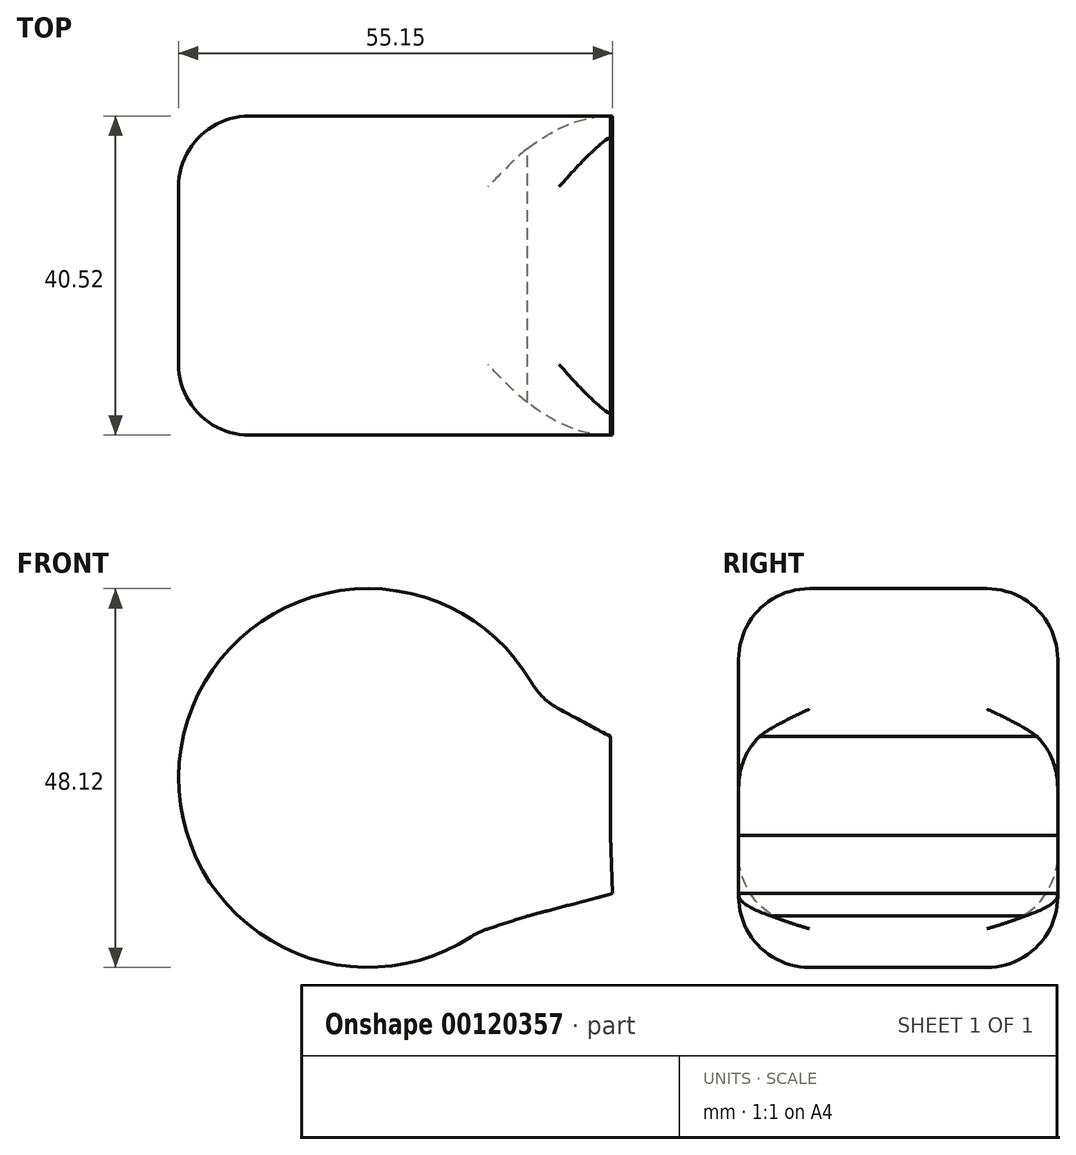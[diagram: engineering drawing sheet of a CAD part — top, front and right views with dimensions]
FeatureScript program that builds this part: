
annotation { "Feature Type Name" : "Feature", "Feature Type Description" : "" }
export const myFeature = defineFeature(function(context is Context, id is Id, definition is map)
    precondition{}
    {
        {
            var Q0;
            Q0=qCreatedBy(makeId("Front.planeOp"),FACE);
            var sketch = newSketch(context, id + "F0", { "sketchPlane" : qUnion([Q0])});
            skCircle(sketch, "E0", {"center": v(0, 0) * mm, "radius": 24.06 * mm});
            skLineSegment(sketch, "E1", {"start": v(21.85, 10.06) * mm, "end": v(30.8, 5.28) * mm});
            skLineSegment(sketch, "E2", {"start": v(30.8, 5.28) * mm, "end": v(30.8, -7.27) * mm});
            skLineSegment(sketch, "E3", {"start": v(30.8, -7.27) * mm, "end": v(31.1, -14.69) * mm});
            skLineSegment(sketch, "E4", {"start": v(31.1, -14.69) * mm, "end": v(20.25, -17.54) * mm});
            skLineSegment(sketch, "E5", {"start": v(20.25, -17.54) * mm, "end": v(14.01, -19.55) * mm});
            skSolve(sketch);
        }
        {
            var Q0;
            Q0 = qSketchRegion(id + "F0", true);
            extrude(context, id + "F1", {"entities" : qUnion([Q0]), "depth" : 40.52 * mm});
        }
        {
            var Q0;
            Q0=makeQuery(id+"F1.opExtrude","SWEPT_FACE",FACE,{"disambiguationData":[OSD([sQuery(id+"F0.wireOp",EDGE,"E0")])]});
            fillet(context, id + "F2", {"entities" : qUnion([Q0]), "radius" : 8.98 * mm, "tangentPropagation" : true, "allowEdgeOverflow" : false});
        }
    });
